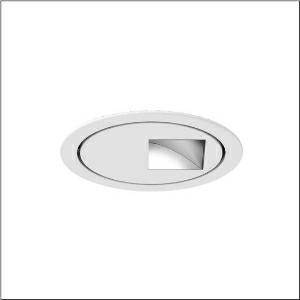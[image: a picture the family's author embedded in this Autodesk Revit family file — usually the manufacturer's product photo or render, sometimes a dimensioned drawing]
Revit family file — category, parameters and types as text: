
# Revit family: lunis_11_mini_round_51dk11b72wg21
name_source: partatom
category: Lighting Fixtures
units: mm (PartAtom-declared; Revit-internal decimal feet)

## family parameters
Cut with Voids When Loaded = No
Host = Face
Light Source = No
Part Type = Normal
Room Calculation Point = No
Round Connector Dimension = Use Diameter
Shared = No

## types (1)
- Lunis 11 mini round (1 x LED 4000K / CRI = 80 (unbekannt), 2470 lm, 4000K)
    Apparent Load = 28 VA
    CIE Flux Codes = 44 77 97 100 100
    Color Rendering = 80
    Color Temperature = 4000K
    Default Elevation = 1800 mm
    Description = Lunis 11 mini round, downlight, light control with wallwasher, of highly reflective aluminium, highly specular, light emission: direct distribution, LED rated luminous flux: 2.470lm, light colour: 840, control gear: ECG, with terminal, 3-pole, mains connection: 220..230V, AC/DC, 0/50..60Hz, LED module, luminaire module, of aluminium, highly specular, white, diameter: 176mm, clamping range: 1..40mm, recessing ring, of plastic, traffic white (RAL 9016), protection rating (complete): IP20, insulation class (complete): insulation class II (safety insulation), certification: CE, permissible ambient temperature for indoor applications: 0..+35°C, packaging unit: 1 piece
    Height = 0 mm  [stored 0 ft]
    Lamp = 1 x LED 4000K / CRI >= 80 (unbekannt)
    Lamp Light Flux = 2470 lm
    Lamp count = 1
    Length = 176 mm
    Luminous efficacy = 88 lm/W
    Manufacturer = Siteco
    ModVariant = No
    Model = 51DK11B72WG21
    Mounting Place = Ceiling
    Mounting Type = Recessed
    Number of Poles = 1
    OnlyDefault = Yes
    Power Factor = 1
    Product Name = Lunis 11 mini round
    Product group = downlight
    ProductGroupID = 401
    Protection Class = Protection class II
    Protection Degree = IP 20
    RLX_Detail_Level = 1
    RLX_Emergency_Light_Flux = 0 lm
    RLX_Emergency_Type = 0
    RLX_Emergency_Type_DB = No
    RlxData = <blob elided: 59417 chars, md5=40759456>
    Socket = socket
    Standby Power = 0 W
    System Light Flux = 2470 lm
    System Power = 28 W
    Type Comments = Product without accessories
    Type Image = l_1004772.jpg
    URL = http://relux.com
    VarID = ---
    Voltage = 0 V
    Weight = 0.00 kg
    Width = 176 mm

note: [stored X ft] marks values corroborated as IEEE doubles in the binary element streams (Revit-internal decimal feet)

## geometry (parser evidence)
native form markers: Blend x4, Sweep x12
no freeform markers — native parametric forms only
